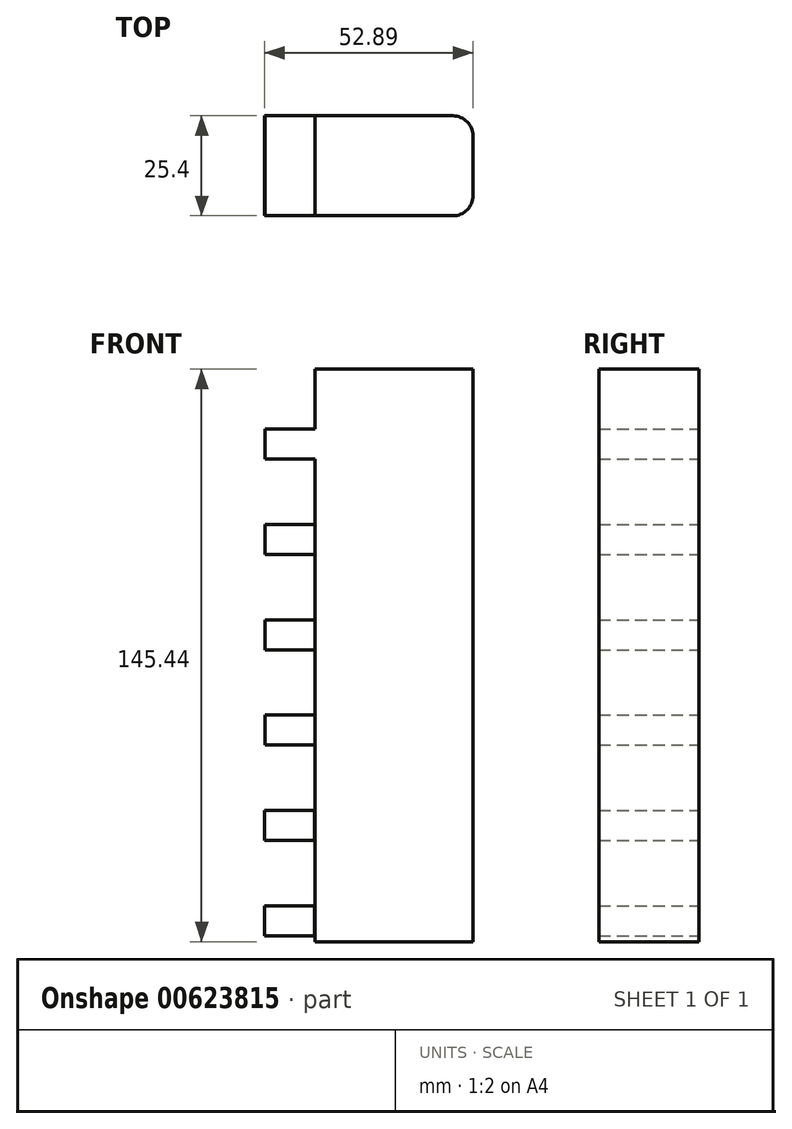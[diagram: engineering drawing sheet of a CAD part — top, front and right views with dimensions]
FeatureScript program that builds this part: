
annotation { "Feature Type Name" : "Feature", "Feature Type Description" : "" }
export const myFeature = defineFeature(function(context is Context, id is Id, definition is map)
    precondition{}
    {
        {
            var Q0;
            Q0=qCreatedBy(makeId("Front.planeOp"),FACE);
            var sketch = newSketch(context, id + "F0", { "sketchPlane" : qUnion([Q0])});
            skLineSegment(sketch, "E0.bottom", {"start": v(20.04, 72.72) * mm, "end": v(-20.04, 72.72) * mm});
            skLineSegment(sketch, "E0.top", {"start": v(20.04, -72.72) * mm, "end": v(-20.04, -72.72) * mm});
            skLineSegment(sketch, "E0.left", {"start": v(20.04, 72.72) * mm, "end": v(20.04, -72.72) * mm});
            skLineSegment(sketch, "E0.right", {"start": v(-20.04, 72.72) * mm, "end": v(-20.04, -72.72) * mm});
            skPoint(sketch, "E0.middle", {"position": v(0, 0) * mm});
            skLineSegment(sketch, "E1.bottom", {"start": v(-20.04, 57.48) * mm, "end": v(-32.74, 57.48) * mm});
            skLineSegment(sketch, "E1.top", {"start": v(-20.04, 49.86) * mm, "end": v(-32.74, 49.86) * mm});
            skLineSegment(sketch, "E1.left", {"start": v(-20.04, 57.48) * mm, "end": v(-20.04, 49.86) * mm});
            skLineSegment(sketch, "E1.right", {"start": v(-32.74, 57.48) * mm, "end": v(-32.74, 49.86) * mm});
            skLineSegment(sketch, "E2.1.0.0", {"start": v(-20.07, 33.27) * mm, "end": v(-32.77, 33.27) * mm});
            skLineSegment(sketch, "E2.1.0.1", {"start": v(-20.07, 25.65) * mm, "end": v(-32.77, 25.65) * mm});
            skLineSegment(sketch, "E2.1.0.2", {"start": v(-20.07, 33.27) * mm, "end": v(-20.07, 25.65) * mm});
            skLineSegment(sketch, "E2.1.0.3", {"start": v(-32.77, 33.27) * mm, "end": v(-32.77, 25.65) * mm});
            skLineSegment(sketch, "E2.2.0.0", {"start": v(-20.09, 9.07) * mm, "end": v(-32.79, 9.07) * mm});
            skLineSegment(sketch, "E2.2.0.1", {"start": v(-20.09, 1.45) * mm, "end": v(-32.79, 1.45) * mm});
            skLineSegment(sketch, "E2.2.0.2", {"start": v(-20.09, 9.07) * mm, "end": v(-20.09, 1.45) * mm});
            skLineSegment(sketch, "E2.2.0.3", {"start": v(-32.79, 9.07) * mm, "end": v(-32.79, 1.45) * mm});
            skLineSegment(sketch, "E2.3.0.0", {"start": v(-20.11, -15.14) * mm, "end": v(-32.81, -15.14) * mm});
            skLineSegment(sketch, "E2.3.0.1", {"start": v(-20.11, -22.76) * mm, "end": v(-32.81, -22.76) * mm});
            skLineSegment(sketch, "E2.3.0.2", {"start": v(-20.11, -15.14) * mm, "end": v(-20.11, -22.76) * mm});
            skLineSegment(sketch, "E2.3.0.3", {"start": v(-32.81, -15.14) * mm, "end": v(-32.81, -22.76) * mm});
            skLineSegment(sketch, "E2.4.0.0", {"start": v(-20.13, -39.35) * mm, "end": v(-32.83, -39.35) * mm});
            skLineSegment(sketch, "E2.4.0.1", {"start": v(-20.13, -46.97) * mm, "end": v(-32.83, -46.97) * mm});
            skLineSegment(sketch, "E2.4.0.2", {"start": v(-20.13, -39.35) * mm, "end": v(-20.13, -46.97) * mm});
            skLineSegment(sketch, "E2.4.0.3", {"start": v(-32.83, -39.35) * mm, "end": v(-32.83, -46.97) * mm});
            skLineSegment(sketch, "E2.5.0.0", {"start": v(-20.15, -63.56) * mm, "end": v(-32.85, -63.56) * mm});
            skLineSegment(sketch, "E2.5.0.1", {"start": v(-20.15, -71.18) * mm, "end": v(-32.85, -71.18) * mm});
            skLineSegment(sketch, "E2.5.0.2", {"start": v(-20.15, -63.56) * mm, "end": v(-20.15, -71.18) * mm});
            skLineSegment(sketch, "E2.5.0.3", {"start": v(-32.85, -63.56) * mm, "end": v(-32.85, -71.18) * mm});
            skLineSegment(sketch, "E2.direction1", {"start": v(-32.74, 57.48) * mm, "end": v(-32.77, 33.27) * mm, "construction": true});
            skSolve(sketch);
        }
        {
            var Q0;
            Q0 = qSketchRegion(id + "F0", true);
            extrude(context, id + "F1", {"entities" : qUnion([Q0]), "depth" : 25.4 * mm, "offsetDistance" : 25.4 * mm});
        }
        {
            var Q0;
            Q0=makeQuery(id+"F1.opExtrude","CAP_EDGE",EDGE,{"disambiguationData":[OSD([sQuery(id+"F0.wireOp",EDGE,"E0.left")])],"isStart":false});
            var Q1;
            Q1=makeQuery(id+"F1.opExtrude","CAP_EDGE",EDGE,{"disambiguationData":[OSD([sQuery(id+"F0.wireOp",EDGE,"E0.left")])],"isStart":true});
            fillet(context, id + "F2", {"entities" : qUnion([Q0, Q1]), "radius" : 5.08 * mm, "tangentPropagation" : true, "allowEdgeOverflow" : false});
        }
    });
